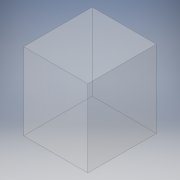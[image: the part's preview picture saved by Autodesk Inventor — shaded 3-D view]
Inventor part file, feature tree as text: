
AUTODESK INVENTOR PART (.ipt)
format: ipt  version: 2017 (Build 210142000, 142)  size: 93,696 bytes
history: native  units: in
note: dims shown in document units (in); Inventor stores cm internally (conversion verified against a paired STEP export)
features: extrude x1, sketch x1
ambient origin geometry x8: Origin, YZ Plane, XZ Plane, XY Plane, X Axis, Y Axis, Z Axis, Center Point
bodies: Solid1 (feature_tree)
feature tree (2):
  extrude  "Extrusion1"  Depth=30.0in
  sketch  "Sketch1"  dims[d0=32.0in d1=30.0in d2=36.0in d3=0.0in]
